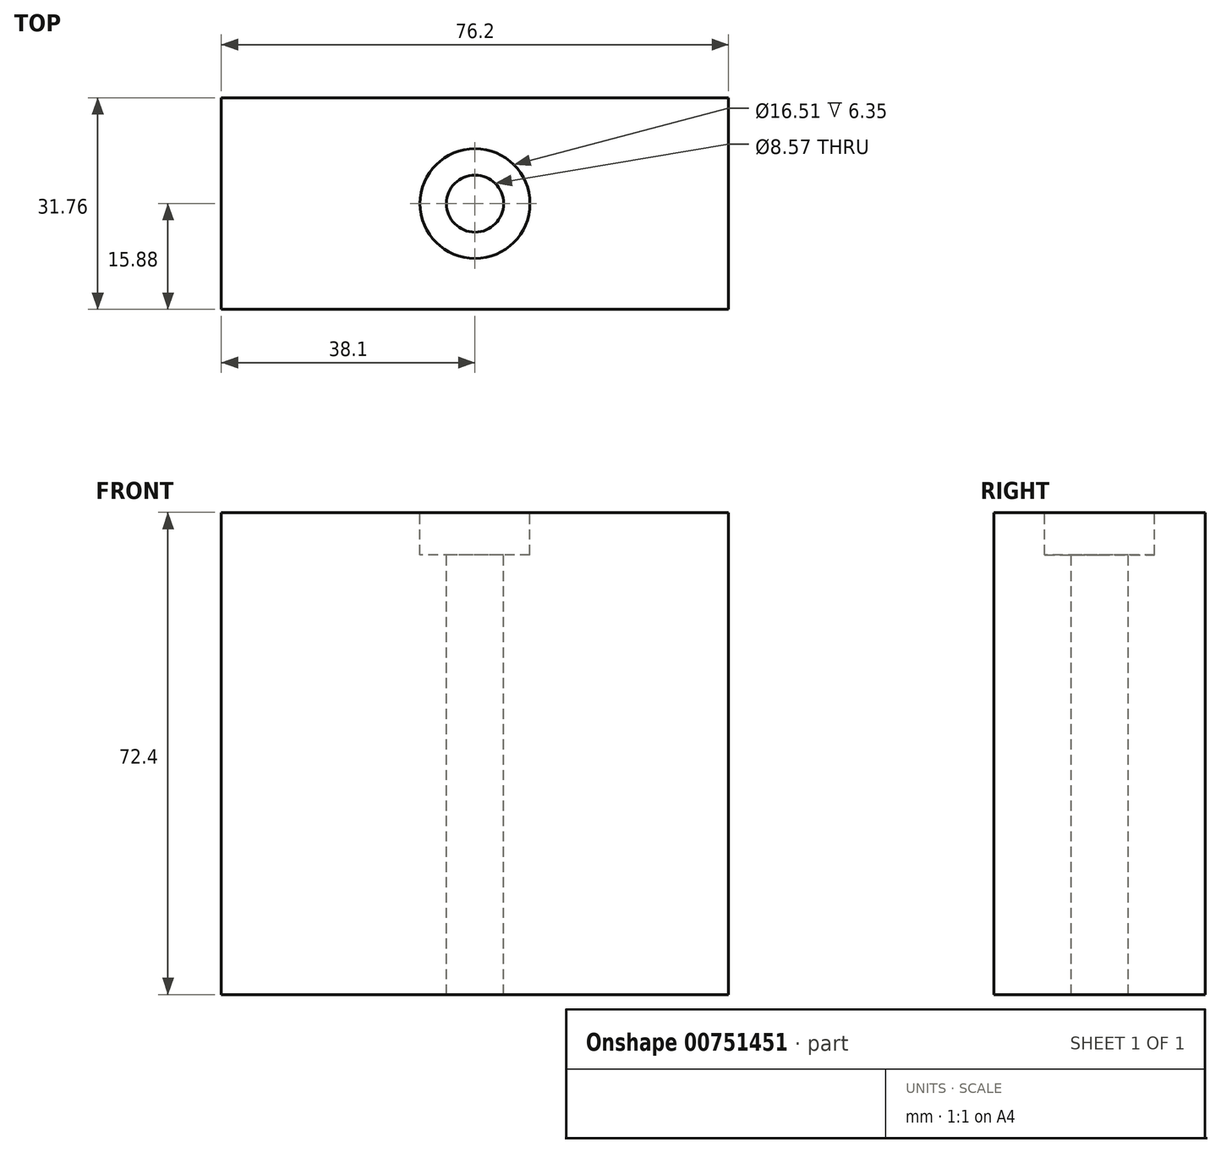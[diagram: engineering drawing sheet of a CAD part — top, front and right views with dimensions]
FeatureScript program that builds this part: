
annotation { "Feature Type Name" : "Feature", "Feature Type Description" : "" }
export const myFeature = defineFeature(function(context is Context, id is Id, definition is map)
    precondition{}
    {
        {
            var Q0;
            Q0=qCreatedBy(makeId("Right.planeOp"),FACE);
            var sketch = newSketch(context, id + "F0", { "sketchPlane" : qUnion([Q0])});
            skLineSegment(sketch, "E0.bottom", {"start": v(-15.88, 36.2) * mm, "end": v(15.88, 36.2) * mm});
            skLineSegment(sketch, "E0.top", {"start": v(-15.88, -36.2) * mm, "end": v(15.88, -36.2) * mm});
            skLineSegment(sketch, "E0.left", {"start": v(-15.87, 36.2) * mm, "end": v(-15.88, -36.2) * mm});
            skLineSegment(sketch, "E0.right", {"start": v(15.88, 36.2) * mm, "end": v(15.87, -36.2) * mm});
            skPoint(sketch, "E1", {"position": v(15.88, 0) * mm});
            skPoint(sketch, "E2", {"position": v(0, -36.2) * mm});
            skSolve(sketch);
        }
        {
            var Q0;
            Q0=makeQuery(id+"F0.imprint","IMPRINT",FACE,{"disambiguationData":[TD([[makeQuery(id+"F0.imprint","IMPRINT",EDGE,{"derivedFrom":sQuery(id+"F0.wireOp",EDGE,"E0.bottom")}),-1.0]])]});
            extrude(context, id + "F1", {"entities" : qUnion([Q0]), "depth" : 38.1 * mm, "offsetDistance" : 25.4 * mm, "hasSecondDirection" : true, "secondDirectionOppositeDirection" : true, "secondDirectionDepth" : 38.1 * mm});
        }
        {
            var Q0;
            Q0=makeQuery(id+"F1.opExtrude","SWEPT_FACE",FACE,{"disambiguationData":[OSD([sQuery(id+"F0.wireOp",EDGE,"E0.bottom")])]});
            var sketch = newSketch(context, id + "F2", { "sketchPlane" : qUnion([Q0])});
            skCircle(sketch, "E3", {"center": v(0, 0) * mm, "radius": 8.26 * mm});
            skCircle(sketch, "E4", {"center": v(0, 0) * mm, "radius": 4.29 * mm});
            skSolve(sketch);
        }
        {
            var Q0;
            Q0=makeQuery(id+"F2.imprint","IMPRINT",FACE,{"disambiguationData":[TD([[makeQuery(id+"F2.imprint","IMPRINT",EDGE,{"derivedFrom":sQuery(id+"F2.wireOp",EDGE,"E3")}),1.0]])]});
            extrude(context, id + "F3", {"entities" : qUnion([Q0]), "operationType" : NewBodyOperationType.REMOVE, "oppositeDirection" : true, "depth" : 6.35 * mm, "offsetDistance" : 25.4 * mm});
        }
        {
            var Q0;
            Q0=makeQuery(id+"F3.boolean.opBoolean","SPLIT",FACE,{"disambiguationData":[TD([makeQuery(id+"F3.opExtrude","SWEPT_FACE",FACE,{"disambiguationData":[OSD([sQuery(id+"F2.wireOp",EDGE,"E4")])]})])],"derivedFrom":makeQuery(id+"F1.opExtrude","SWEPT_FACE",FACE,{"disambiguationData":[OSD([sQuery(id+"F0.wireOp",EDGE,"E0.bottom")])]})});
            extrude(context, id + "F4", {"entities" : qUnion([Q0]), "operationType" : NewBodyOperationType.REMOVE, "endBound" : BoundingType.THROUGH_ALL, "oppositeDirection" : true, "depth" : 25.4 * mm, "offsetDistance" : 25.4 * mm});
        }
    });
